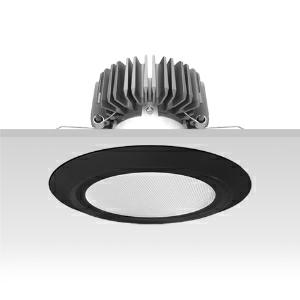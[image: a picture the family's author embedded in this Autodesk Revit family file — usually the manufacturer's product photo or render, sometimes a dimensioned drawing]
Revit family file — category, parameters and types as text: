
# Revit family: 3f_filippi_-_3f_reno_bianco_ampio_3f_filippi_-_30675_a01038_-_3f_reno_200_wh_2000-930_dali_wide___vs_bk_0945
name_source: partatom
category: Lighting Fixtures
units: mm (PartAtom-declared; Revit-internal decimal feet)

## family parameters
Cut with Voids When Loaded = No
Host = Face
Light Source = No
Part Type = Normal
Room Calculation Point = No
Round Connector Dimension = Use Diameter
Shared = No

## types (1)
- 3F Filippi - 3F Reno Bianco Ampio (1 x LED, 1650 lm, 24 W, 3000 K)
    Apparent Load = 24 VA
    Approval mark = CE
    CIE Flux Codes = 75 94 99 100 100
    Color Rendering = 90
    Color Temperature = 3000 K
    Control Gear = Electronic transformer
    Default Elevation = 1800 mm
    Description = ILLUMINOTECHNICAL
Luminous efficiency 100% (DLOR 100%, ULOR 0%).
Initial luminous flux of the luminaire 1650 lm.
Direct symmetric wide distribution.
Installation Interdistance Transv.D = 1.16 x hu - Long.D = 1.14 x hu.
Average luminance <3000 cd/m² for radial angles >65°.
Tabular UGR (CIE 117 - 4H-8H; S=0.25H; 70/50/20): RUG 20.3 - 20.2.
Beam angle: 74° - 74°.
Luminous efficacy 69 lm/W.
Lifetime (L90/B10): 30000 h. (tq+25°C)
Lifetime (L85/B10): 50000 h. (tq+25°C)
Lifetime (L70/B10): 80000 h. (tq+25°C)
Sudden decreased luminous flux after 50000 hours: 0% (C0).
Photobiological safety in compliance with IEC/TR 62778: RG0 risk exempt, (IEC 62471).
In compliance with IEC/EN 62722-2-1 - IEC/EN 62717 standards.

SOURCE
Compact LED module 2000/930.
Energy efficiency class (UE 2019/2020 - UE 2019/2015): E.
CIE 13.3 Colour rendering index: CRI >90 (R9 >50%).
IES TM-30 Fidelity Index: Rf = 92 Rg = 101.
CCT nominal colour temperature 3000 K.
Colour initial tolerance (MacAdam): SDCM 3.
Zhaga Book 3 compliant.

MECHANICAL
Passive heat dissipator in die-casting aluminium, oversized, for optimum thermal management of the LED module.
Parabolic element with graduated/concentric rings in white polycarbonate.
Transparent external lens with glossy and satin differentiated surfaces, with a cooling and anti-insect system in methacrylate (PMMA).
Fastening spring clips in stainless steel.
Dimensions: diameter 226 mm, height 146 mm. Weight 1.17 kg.
IP44 protection degree for exposed part, IP20 for recessed part.
Mechanical strength to impacts IK06 (1 joule).
Glow-wire test resistance 650°C.

ELECTRICAL
Wiring on a separate unit.
Halogen Free DALI-2 DATI (Parts 251, 252, 253), PUSH-DIM, electronic wiring 230V-50/60Hz, power factor 0.95 at full load, THD <25%, constant output current, SELV, class II, 1 driver, 1 DALI addresse.
Power of the luminaire 24 W.
ENEC - CE.
SAFE FLICKER: PstLM=<1 and SVM=<0.4 (IEC TR 61547-1 and IEC TR 63158), to ensure a more comfortable and safe light.
Luminaire compliant with EN 60598-2-22 for power supply from a centralised emergency system CPSS (Central Power Supply System), not incorporated in the luminaire - high risk areas excluded. The default power and flux are 100% in AC and 100% in DC.
Ambient temperature from 0°C to +25°C.
Temperature class T6 max 85°C.
Relative humidity UR: <85%.

INSTALLATION
Pull-up recessed fitting.
False ceiling carving: 200 mm.
All accessories dedicated to this product are available on the Catalog and on our website www.3F-Filippi.com.

ACCESSORIES
A01038 - Anti-glare microprismatic VS moulded glass, tempered, not flammable, locked and in line with the trim, in black polycarbonate.

APPLICATIONS
Environments: architectural, commercial, exhibition areas, transit areas, corridors, shops, display windows, service areas.
In false ceilings with narrow voids.

LIGHT MANAGEMENT
Recommended minimum setting: 10%.
The luminaire, equipped with (DALI-2 DATI) driver, can be controlled manually with 3F Easy Dim technology or automatically/manually with wired or wireless DALI/D2D control systems.
The D2D driver guarantees interoperability with other devices with the same certification by making the following information available:
Device Data (Part 251), Energy Report (Part 252), Diagnosis & Maintenance (Part 253).
In electrical systems without a regulation system (manual or automatic) and DALI bus, a suitable jumper must be made on the DA-DA terminals of the appliance.

WARNING
Luminaire designed for disposal/recycling at end-of-life.
Replaceable (LED only) light source by a professional. Replaceable control gear by a professional.
    Height = 0 mm  [stored 0 ft]
    Lamp = 1 x LED
    Lamp Light Flux = 1650 lm
    Lamp Power = 24 W
    Lamp count = 1
    Length = 226 mm
    Lifetime = 50000 h
    Luminous efficacy = 69 lm/W
    Manufacturer = 3F Filippi
    ModVariant = No
    Model = 3F Filippi - 30675+A01038 - 3F Reno 200 WH 2000-930 DALI WIDE + VS BK
    Mounting Place = Ceiling
    Mounting Type = Recessed
    Number of Poles = 1
    OnlyDefault = Yes
    Power Factor = 1
    Product Name = 3F Filippi - 3F Reno Bianco Ampio
    Product group = recessed luminaire
    ProductGroupID = 4
    Protection Class = Protection class II
    Protection Degree = IP 20
    RLX_Detail_Level = 1
    RLX_Emergency_Light_Flux = 0 lm
    RLX_Emergency_Type = 0
    RLX_Emergency_Type_DB = No
    RlxData = <blob elided: 99333 chars, md5=c8b51a78>
    Socket = socket
    Standby Power = 0 W
    System Light Flux = 1650 lm
    System Power = 24 W
    Type Comments = Product without accessories
    Type Image = 3ffilippi_3f_reno_200_bk_vs_smp.jpg
    URL = http://relux.com
    VarID = ---
    Voltage = 0 V
    Weight = 0.00 kg
    Width = 0 mm  [stored 0 ft]

note: [stored X ft] marks values corroborated as IEEE doubles in the binary element streams (Revit-internal decimal feet)

## geometry (parser evidence)
native form markers: Blend x4, Sweep x9
no freeform markers — native parametric forms only
